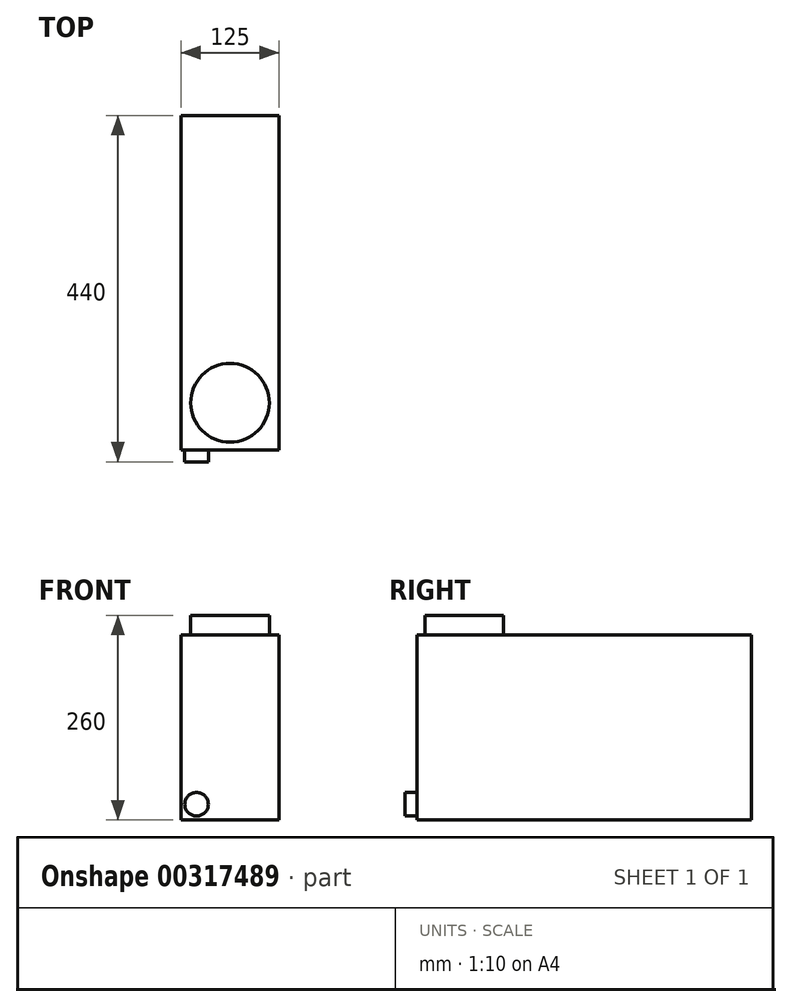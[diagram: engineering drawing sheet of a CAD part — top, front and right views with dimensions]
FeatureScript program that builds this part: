
annotation { "Feature Type Name" : "Feature", "Feature Type Description" : "" }
export const myFeature = defineFeature(function(context is Context, id is Id, definition is map)
    precondition{}
    {
        {
            var Q0;
            Q0=qCreatedBy(makeId("Top.planeOp"),FACE);
            var sketch = newSketch(context, id + "F0", { "sketchPlane" : qUnion([Q0])});
            skLineSegment(sketch, "E0.bottom", {"start": v(62.5, -212.5) * mm, "end": v(-62.5, -212.5) * mm});
            skLineSegment(sketch, "E0.top", {"start": v(62.5, 212.5) * mm, "end": v(-62.5, 212.5) * mm});
            skLineSegment(sketch, "E0.left", {"start": v(62.5, -212.5) * mm, "end": v(62.5, 212.5) * mm});
            skLineSegment(sketch, "E0.right", {"start": v(-62.5, -212.5) * mm, "end": v(-62.5, 212.5) * mm});
            skPoint(sketch, "E0.middle", {"position": v(0, 0) * mm});
            skSolve(sketch);
        }
        {
            var Q0;
            Q0 = qSketchRegion(id + "F0", true);
            extrude(context, id + "F1", {"entities" : qUnion([Q0]), "depth" : 235 * mm});
        }
        {
            var Q0;
            Q0=makeQuery(id+"F1.opExtrude","SWEPT_FACE",FACE,{"disambiguationData":[OSD([sQuery(id+"F0.wireOp",EDGE,"E0.bottom")])]});
            var sketch = newSketch(context, id + "F2", { "sketchPlane" : qUnion([Q0])});
            skCircle(sketch, "E1", {"center": v(-42.5, 20) * mm, "radius": 15 * mm});
            skSolve(sketch);
        }
        {
            var Q0;
            Q0 = qSketchRegion(id + "F2", true);
            extrude(context, id + "F3", {"entities" : qUnion([Q0]), "operationType" : NewBodyOperationType.ADD, "depth" : 15 * mm});
        }
        {
            var Q0;
            Q0=makeQuery(id+"F1.opExtrude","CAP_FACE",FACE,{"disambiguationData":[OSD([sQuery(id+"F0.wireOp",EDGE,"E0.bottom"),sQuery(id+"F0.wireOp",EDGE,"E0.top"),sQuery(id+"F0.wireOp",EDGE,"E0.left"),sQuery(id+"F0.wireOp",EDGE,"E0.right")])],"isStart":false});
            var sketch = newSketch(context, id + "F4", { "sketchPlane" : qUnion([Q0])});
            skCircle(sketch, "E2", {"center": v(0, -152.5) * mm, "radius": 50 * mm});
            skPoint(sketch, "E2.centerSnap0", {"position": v(0, -212.5) * mm});
            skSolve(sketch);
        }
        {
            var Q0;
            Q0 = qSketchRegion(id + "F4", true);
            extrude(context, id + "F5", {"entities" : qUnion([Q0]), "operationType" : NewBodyOperationType.ADD, "depth" : 25 * mm});
        }
    });
